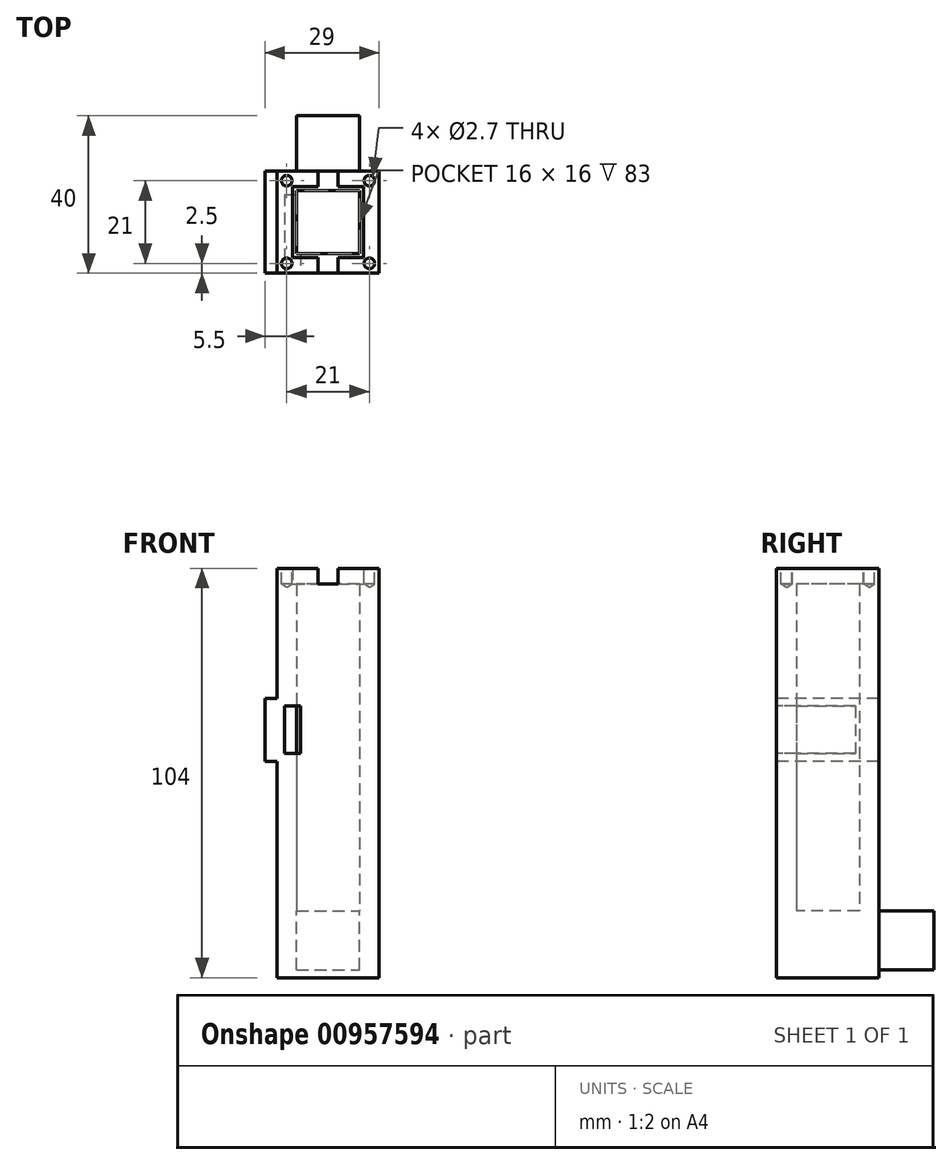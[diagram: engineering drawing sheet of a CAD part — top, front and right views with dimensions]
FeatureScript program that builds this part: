
annotation { "Feature Type Name" : "Feature", "Feature Type Description" : "" }
export const myFeature = defineFeature(function(context is Context, id is Id, definition is map)
    precondition{}
    {
        {
            var Q0;
            Q0=qCreatedBy(makeId("Top.planeOp"),FACE);
            var sketch = newSketch(context, id + "F0", { "sketchPlane" : qUnion([Q0])});
            skLineSegment(sketch, "E0.bottom", {"start": v(13, 13) * mm, "end": v(-13, 13) * mm});
            skLineSegment(sketch, "E0.top", {"start": v(13, -13) * mm, "end": v(-13, -13) * mm});
            skLineSegment(sketch, "E0.left", {"start": v(13, 13) * mm, "end": v(13, -13) * mm});
            skLineSegment(sketch, "E0.right", {"start": v(-13, 13) * mm, "end": v(-13, -13) * mm});
            skPoint(sketch, "E0.middle", {"position": v(0, 0) * mm});
            skLineSegment(sketch, "E1.bottom", {"start": v(8, 8) * mm, "end": v(-8, 8) * mm});
            skLineSegment(sketch, "E1.top", {"start": v(8, -8) * mm, "end": v(-8, -8) * mm});
            skLineSegment(sketch, "E1.left", {"start": v(8, 8) * mm, "end": v(8, -8) * mm});
            skLineSegment(sketch, "E1.right", {"start": v(-8, 8) * mm, "end": v(-8, -8) * mm});
            skSolve(sketch);
        }
        {
            var Q0;
            Q0=makeQuery(id+"F0.imprint","IMPRINT",FACE,{"disambiguationData":[TD([[makeQuery(id+"F0.imprint","IMPRINT",EDGE,{"derivedFrom":sQuery(id+"F0.wireOp",EDGE,"E0.bottom")}),1.0]])]});
            var Q1;
            Q1=makeQuery(id+"F0.imprint","IMPRINT",FACE,{"disambiguationData":[TD([[makeQuery(id+"F0.imprint","IMPRINT",EDGE,{"derivedFrom":sQuery(id+"F0.wireOp",EDGE,"E1.bottom")}),-1.0]])]});
            var Q2;
            Q2=makeQuery(id+"F0.imprint","IMPRINT",FACE,{"disambiguationData":[TD([[makeQuery(id+"F0.imprint","IMPRINT",EDGE,{"derivedFrom":sQuery(id+"F0.wireOp",EDGE,"E1.bottom")}),1.0]])]});
            extrude(context, id + "F1", {"entities" : qUnion([Q0, Q1, Q2]), "depth" : 2 * mm, "offsetDistance" : 25 * mm});
        }
        {
            var Q0;
            Q0=qSketchRegion(id+"F0",true);
            var Q1;
            Q1=makeQuery(id+"F0.imprint","IMPRINT",FACE,{"disambiguationData":[TD([[makeQuery(id+"F0.imprint","IMPRINT",EDGE,{"derivedFrom":sQuery(id+"F0.wireOp",EDGE,"E1.bottom")}),-1.0]])]});
            extrude(context, id + "F2", {"entities" : qUnion([Q0, Q1]), "operationType" : NewBodyOperationType.ADD, "depth" : 100 * mm, "offsetDistance" : 25 * mm});
        }
        {
            var Q0;
            Q0=makeQuery(id+"F2.opExtrude","CAP_FACE",FACE,{"disambiguationData":[OSD([sQuery(id+"F0.wireOp",EDGE,"E0.bottom"),sQuery(id+"F0.wireOp",EDGE,"E0.top"),sQuery(id+"F0.wireOp",EDGE,"E0.left"),sQuery(id+"F0.wireOp",EDGE,"E0.right"),sQuery(id+"F0.wireOp",EDGE,"E1.bottom"),sQuery(id+"F0.wireOp",EDGE,"E1.top"),sQuery(id+"F0.wireOp",EDGE,"E1.left"),sQuery(id+"F0.wireOp",EDGE,"E1.right")])],"isStart":false});
            var sketch = newSketch(context, id + "F3", { "sketchPlane" : qUnion([Q0])});
            skLineSegment(sketch, "E2.bottom", {"start": v(-9, 9) * mm, "end": v(9, 9) * mm});
            skLineSegment(sketch, "E2.top", {"start": v(-9, -9) * mm, "end": v(9, -9) * mm});
            skLineSegment(sketch, "E2.left", {"start": v(-9, 9) * mm, "end": v(-9, -9) * mm});
            skLineSegment(sketch, "E2.right", {"start": v(9, 9) * mm, "end": v(9, -9) * mm});
            skPoint(sketch, "E2.middle", {"position": v(0, 0) * mm});
            skSolve(sketch);
        }
        {
            var Q0;
            Q0=makeQuery(id+"F3.imprint","IMPRINT",FACE,{"disambiguationData":[TD([[makeQuery(id+"F3.imprint","IMPRINT",EDGE,{"derivedFrom":sQuery(id+"F3.wireOp",EDGE,"E2.bottom")}),1.0]])]});
            extrude(context, id + "F4", {"entities" : qUnion([Q0]), "operationType" : NewBodyOperationType.ADD, "depth" : 4 * mm, "offsetDistance" : 25 * mm});
        }
        {
            var Q0;
            Q0=makeQuery(id+"F4.opExtrude","CAP_FACE",FACE,{"disambiguationData":[OSD([sQuery(id+"F0.wireOp",EDGE,"E0.bottom"),sQuery(id+"F0.wireOp",EDGE,"E0.top"),sQuery(id+"F0.wireOp",EDGE,"E0.left"),sQuery(id+"F0.wireOp",EDGE,"E0.right"),sQuery(id+"F3.wireOp",EDGE,"E2.bottom"),sQuery(id+"F3.wireOp",EDGE,"E2.top"),sQuery(id+"F3.wireOp",EDGE,"E2.left"),sQuery(id+"F3.wireOp",EDGE,"E2.right")])],"isStart":false});
            var sketch = newSketch(context, id + "F5", { "sketchPlane" : qUnion([Q0])});
            skLineSegment(sketch, "E3", {"start": v(-2.5, 13) * mm, "end": v(-2.5, 9) * mm});
            skLineSegment(sketch, "E4.MirrorCS", {"start": v(2.5, 13) * mm, "end": v(2.5, 9) * mm});
            skLineSegment(sketch, "E5.MirrorCS", {"start": v(2.5, -13) * mm, "end": v(2.5, -9) * mm});
            skLineSegment(sketch, "E6.MirrorCS", {"start": v(-2.5, -13) * mm, "end": v(-2.5, -9) * mm});
            skLineSegment(sketch, "E7", {"start": v(-13, 13) * mm, "end": v(-9, 9) * mm, "construction": true});
            skPoint(sketch, "E8", {"position": v(-10.5, 10.5) * mm});
            skPoint(sketch, "E9.MirrorP", {"position": v(10.5, 10.5) * mm});
            skLineSegment(sketch, "E10.MirrorCS", {"start": v(13, 13) * mm, "end": v(9, 9) * mm, "construction": true});
            skLineSegment(sketch, "E11.MirrorCS", {"start": v(-13, -13) * mm, "end": v(-9, -9) * mm, "construction": true});
            skPoint(sketch, "E12.MirrorP", {"position": v(-10.5, -10.5) * mm});
            skLineSegment(sketch, "E13.MirrorCS", {"start": v(13, -13) * mm, "end": v(9, -9) * mm, "construction": true});
            skPoint(sketch, "E14.MirrorP", {"position": v(10.5, -10.5) * mm});
            skSolve(sketch);
        }
        {
            var Q0;
            {var subQ0=sQuery(id+"F5.wireOp",EDGE,"E5.MirrorCS");Q0=makeQuery(id+"F5.imprint","IMPRINT",FACE,{"disambiguationData":[TD([[makeQuery(id+"F5.imprint","IMPRINT",EDGE,{"derivedFrom":subQ0}),1.0]])]});}
            var Q1;
            {var subQ0=sQuery(id+"F5.wireOp",EDGE,"E3");Q1=makeQuery(id+"F5.imprint","IMPRINT",FACE,{"disambiguationData":[TD([[makeQuery(id+"F5.imprint","IMPRINT",EDGE,{"derivedFrom":subQ0}),1.0]])]});}
            var Q2;
            Q2=makeQuery(id+"F2.opExtrude","CAP_FACE",FACE,{"disambiguationData":[OSD([sQuery(id+"F0.wireOp",EDGE,"E0.bottom"),sQuery(id+"F0.wireOp",EDGE,"E0.top"),sQuery(id+"F0.wireOp",EDGE,"E0.left"),sQuery(id+"F0.wireOp",EDGE,"E0.right"),sQuery(id+"F0.wireOp",EDGE,"E1.bottom"),sQuery(id+"F0.wireOp",EDGE,"E1.top"),sQuery(id+"F0.wireOp",EDGE,"E1.left"),sQuery(id+"F0.wireOp",EDGE,"E1.right")])],"isStart":false});
            extrude(context, id + "F6", {"entities" : qUnion([Q0, Q1]), "operationType" : NewBodyOperationType.REMOVE, "endBound" : BoundingType.UP_TO_SURFACE, "oppositeDirection" : true, "depth" : 25 * mm, "endBoundEntityFace" : qUnion([Q2]), "offsetDistance" : 25 * mm});
        }
        {
            var Q0;
            Q0=sQuery(id+"F5.wireOp",VERTEX,"E8");
            var Q1;
            Q1=sQuery(id+"F5.wireOp",VERTEX,"E9.MirrorP");
            var Q2;
            Q2=sQuery(id+"F5.wireOp",VERTEX,"E12.MirrorP");
            var Q3;
            Q3=sQuery(id+"F5.wireOp",VERTEX,"E14.MirrorP");
            var Q4;
            Q4=makeQuery(id+"F1.opExtrude","SWEPT_BODY",BODY,{"disambiguationData":[OSD([sQuery(id+"F0.wireOp",EDGE,"E0.bottom"),sQuery(id+"F0.wireOp",EDGE,"E0.top"),sQuery(id+"F0.wireOp",EDGE,"E0.left"),sQuery(id+"F0.wireOp",EDGE,"E0.right")])]});
            hole(context, id + "F7", {"style" : HoleStyle.SIMPLE, "endStyle" : HoleEndStyle.BLIND, "standardTappedOrClearance" : lookupTablePath({ "standard" : "ISO", "engagement" : "50%", "pitch" : "0.5 mm", "size" : "M3", "type" : "Tapped" }), "standardBlindInLast" : lookupTablePath({ "standard" : "ISO", "fit" : "Normal", "engagement" : "50%", "pitch" : "0.5 mm", "size" : "M3", "type" : "Clearance & tapped" }), "holeDiameter" : 2.7 * mm, "majorDiameter" : 3 * mm, "showTappedDepth" : true, "holeDepth" : 4 * mm, "isTappedThrough" : true, "tappedDepth" : 2.5 * mm, "tapClearance" : 3, "locations" : qUnion([Q0, Q1, Q2, Q3]), "scope" : qUnion([Q4])});
        }
        {
            var Q0;
            {var subQ0=sQuery(id+"F0.wireOp",EDGE,"E0.left");Q0=makeQuery(id+"F4.boolean.opBoolean","MERGE",FACE,{"derivedFrom":[makeQuery(id+"F2.boolean.opBoolean","MERGE",FACE,{"derivedFrom":[makeQuery(id+"F1.opExtrude","SWEPT_FACE",FACE,{"disambiguationData":[OSD([subQ0])]}),makeQuery(id+"F2.opExtrude","SWEPT_FACE",FACE,{"disambiguationData":[OSD([subQ0])]})]}),makeQuery(id+"F4.opExtrude","SWEPT_FACE",FACE,{"disambiguationData":[OSD([subQ0])]})]});}
            var sketch = newSketch(context, id + "F8", { "sketchPlane" : qUnion([Q0])});
            skLineSegment(sketch, "E15.bottom", {"start": v(-7.98, 98) * mm, "end": v(8.02, 98) * mm});
            skLineSegment(sketch, "E15.top", {"start": v(-7.98, 2) * mm, "end": v(8.02, 2) * mm});
            skLineSegment(sketch, "E15.left", {"start": v(-7.98, 98) * mm, "end": v(-7.98, 2) * mm});
            skLineSegment(sketch, "E15.right", {"start": v(8.02, 98) * mm, "end": v(8.02, 2) * mm});
            skLineSegment(sketch, "E16", {"start": v(-7.98, 0) * mm, "end": v(-7.98, 100) * mm, "construction": true});
            skLineSegment(sketch, "E17", {"start": v(8.02, 0) * mm, "end": v(8.02, 100) * mm, "construction": true});
            skSolve(sketch);
        }
        {
            var Q0;
            {var subQ0=sQuery(id+"F0.wireOp",EDGE,"E0.top");Q0=makeQuery(id+"F4.boolean.opBoolean","MERGE",FACE,{"derivedFrom":[makeQuery(id+"F2.boolean.opBoolean","MERGE",FACE,{"derivedFrom":[makeQuery(id+"F1.opExtrude","SWEPT_FACE",FACE,{"disambiguationData":[OSD([subQ0])]}),makeQuery(id+"F2.opExtrude","SWEPT_FACE",FACE,{"disambiguationData":[OSD([subQ0])]})]}),makeQuery(id+"F4.opExtrude","SWEPT_FACE",FACE,{"disambiguationData":[OSD([subQ0])]})]});}
            var sketch = newSketch(context, id + "F9", { "sketchPlane" : qUnion([Q0])});
            skLineSegment(sketch, "E18.bottom", {"start": v(-13, 55) * mm, "end": v(-16, 55) * mm});
            skLineSegment(sketch, "E18.top", {"start": v(-13, 71) * mm, "end": v(-16, 71) * mm});
            skLineSegment(sketch, "E18.left", {"start": v(-13, 71) * mm, "end": v(-13, 55) * mm});
            skLineSegment(sketch, "E18.right", {"start": v(-16, 71) * mm, "end": v(-16, 55) * mm});
            skSolve(sketch);
        }
        {
            var Q0;
            Q0 = qSketchRegion(id + "F9", true);
            extrude(context, id + "F10", {"entities" : qUnion([Q0]), "operationType" : NewBodyOperationType.ADD, "oppositeDirection" : true, "depth" : 26 * mm, "offsetDistance" : 25 * mm});
        }
        {
            var Q0;
            {var subQ0=sQuery(id+"F0.wireOp",EDGE,"E0.top");Q0=makeQuery(id+"F10.boolean.opBoolean","MERGE",FACE,{"derivedFrom":[makeQuery(id+"F4.boolean.opBoolean","MERGE",FACE,{"derivedFrom":[makeQuery(id+"F2.boolean.opBoolean","MERGE",FACE,{"derivedFrom":[makeQuery(id+"F1.opExtrude","SWEPT_FACE",FACE,{"disambiguationData":[OSD([subQ0])]}),makeQuery(id+"F2.opExtrude","SWEPT_FACE",FACE,{"disambiguationData":[OSD([subQ0])]})]}),makeQuery(id+"F4.opExtrude","SWEPT_FACE",FACE,{"disambiguationData":[OSD([subQ0])]})]}),makeQuery(id+"F10.opExtrude","CAP_FACE",FACE,{"disambiguationData":[OSD([sQuery(id+"F9.wireOp",EDGE,"E18.bottom"),sQuery(id+"F9.wireOp",EDGE,"E18.top"),sQuery(id+"F9.wireOp",EDGE,"E18.left"),sQuery(id+"F9.wireOp",EDGE,"E18.right")])],"isStart":true})]});}
            var sketch = newSketch(context, id + "F11", { "sketchPlane" : qUnion([Q0])});
            skLineSegment(sketch, "E19.bottom", {"start": v(-11, 69) * mm, "end": v(-7, 69) * mm});
            skLineSegment(sketch, "E19.top", {"start": v(-11, 57) * mm, "end": v(-7, 57) * mm});
            skLineSegment(sketch, "E19.left", {"start": v(-11, 69) * mm, "end": v(-11, 57) * mm});
            skLineSegment(sketch, "E19.right", {"start": v(-7, 69) * mm, "end": v(-7, 57) * mm});
            skSolve(sketch);
        }
        {
            var Q0;
            Q0 = qSketchRegion(id + "F11", true);
            extrude(context, id + "F12", {"entities" : qUnion([Q0]), "operationType" : NewBodyOperationType.REMOVE, "oppositeDirection" : true, "depth" : 20 * mm, "offsetDistance" : 25 * mm});
        }
        {
            var Q0;
            {var subQ0=sQuery(id+"F0.wireOp",EDGE,"E0.top");Q0=makeQuery(id+"F10.boolean.opBoolean","MERGE",FACE,{"derivedFrom":[makeQuery(id+"F4.boolean.opBoolean","MERGE",FACE,{"derivedFrom":[makeQuery(id+"F2.boolean.opBoolean","MERGE",FACE,{"derivedFrom":[makeQuery(id+"F1.opExtrude","SWEPT_FACE",FACE,{"disambiguationData":[OSD([subQ0])]}),makeQuery(id+"F2.opExtrude","SWEPT_FACE",FACE,{"disambiguationData":[OSD([subQ0])]})]}),makeQuery(id+"F4.opExtrude","SWEPT_FACE",FACE,{"disambiguationData":[OSD([subQ0])]})]}),makeQuery(id+"F10.opExtrude","CAP_FACE",FACE,{"disambiguationData":[OSD([sQuery(id+"F9.wireOp",EDGE,"E18.bottom"),sQuery(id+"F9.wireOp",EDGE,"E18.top"),sQuery(id+"F9.wireOp",EDGE,"E18.left"),sQuery(id+"F9.wireOp",EDGE,"E18.right")])],"isStart":true})]});}
            var sketch = newSketch(context, id + "F13", { "sketchPlane" : qUnion([Q0])});
            skLineSegment(sketch, "E20.bottom", {"start": v(-8, 2) * mm, "end": v(8, 2) * mm});
            skLineSegment(sketch, "E20.top", {"start": v(-8, 17) * mm, "end": v(8, 17) * mm});
            skLineSegment(sketch, "E20.left", {"start": v(-8, 2) * mm, "end": v(-8, 17) * mm});
            skLineSegment(sketch, "E20.right", {"start": v(8, 2) * mm, "end": v(8, 17) * mm});
            skSolve(sketch);
        }
        {
            var Q0;
            Q0 = qSketchRegion(id + "F13", true);
            extrude(context, id + "F14", {"entities" : qUnion([Q0]), "operationType" : NewBodyOperationType.ADD, "oppositeDirection" : true, "depth" : 40 * mm, "offsetDistance" : 25 * mm});
        }
    });
